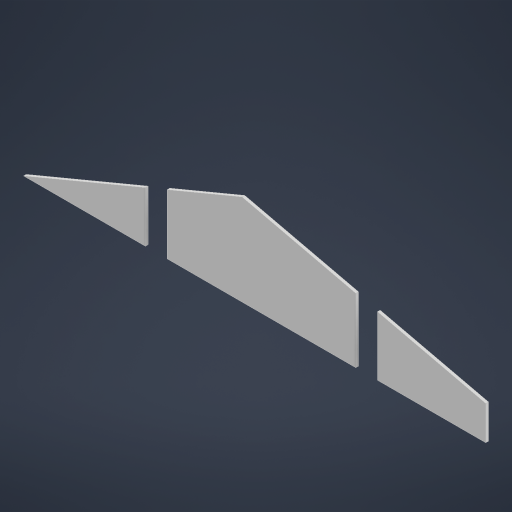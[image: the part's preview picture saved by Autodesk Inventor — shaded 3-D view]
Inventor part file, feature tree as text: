
AUTODESK INVENTOR PART (.ipt)
format: ipt  version: 2023.2 (Build 272271000, 271)  size: 268,288 bytes
history: native  units: mm
features: sketch x1
ambient origin geometry x8: Origin, YZ Plane, XZ Plane, XY Plane, X Axis, Y Axis, Z Axis, Center Point
bodies: Body1 (feature_tree)
feature tree (1):
  sketch  "Sketch1"  dims[d228=105.0deg d268=60.0mm d269=70.0mm d270=300.0mm d273=120.0mm d274=50.0mm d275=105.0deg d283=90.0mm d284=40.0mm d285=45.0mm d289=8.0mm d290=8.0mm d305=2.5mm d306=0.0mm d307=1.5mm d308=0.0mm d9=0.5mm d10=0.872665mm d11=0.5mm d12=0.872665mm d13=0.5mm d14=0.872665mm d27=0.5mm d28=0.872665mm d29=0.5mm d30=0.872665mm d88=0.5mm d89=0.872665mm d90=0.5mm d91=0.872665mm d116=0.5mm d117=0.872665mm d118=0.5mm d119=0.872665mm d154=0.5mm d155=0.872665mm d156=0.5mm d157=0.872665mm d181=0.5mm d182=0.872665mm d183=0.5mm d184=0.872665mm d221=0.5mm d222=0.872665mm d223=0.5mm d224=0.872665mm d301=0.5mm d302=0.872665mm d303=0.5mm d304=0.872665mm]
